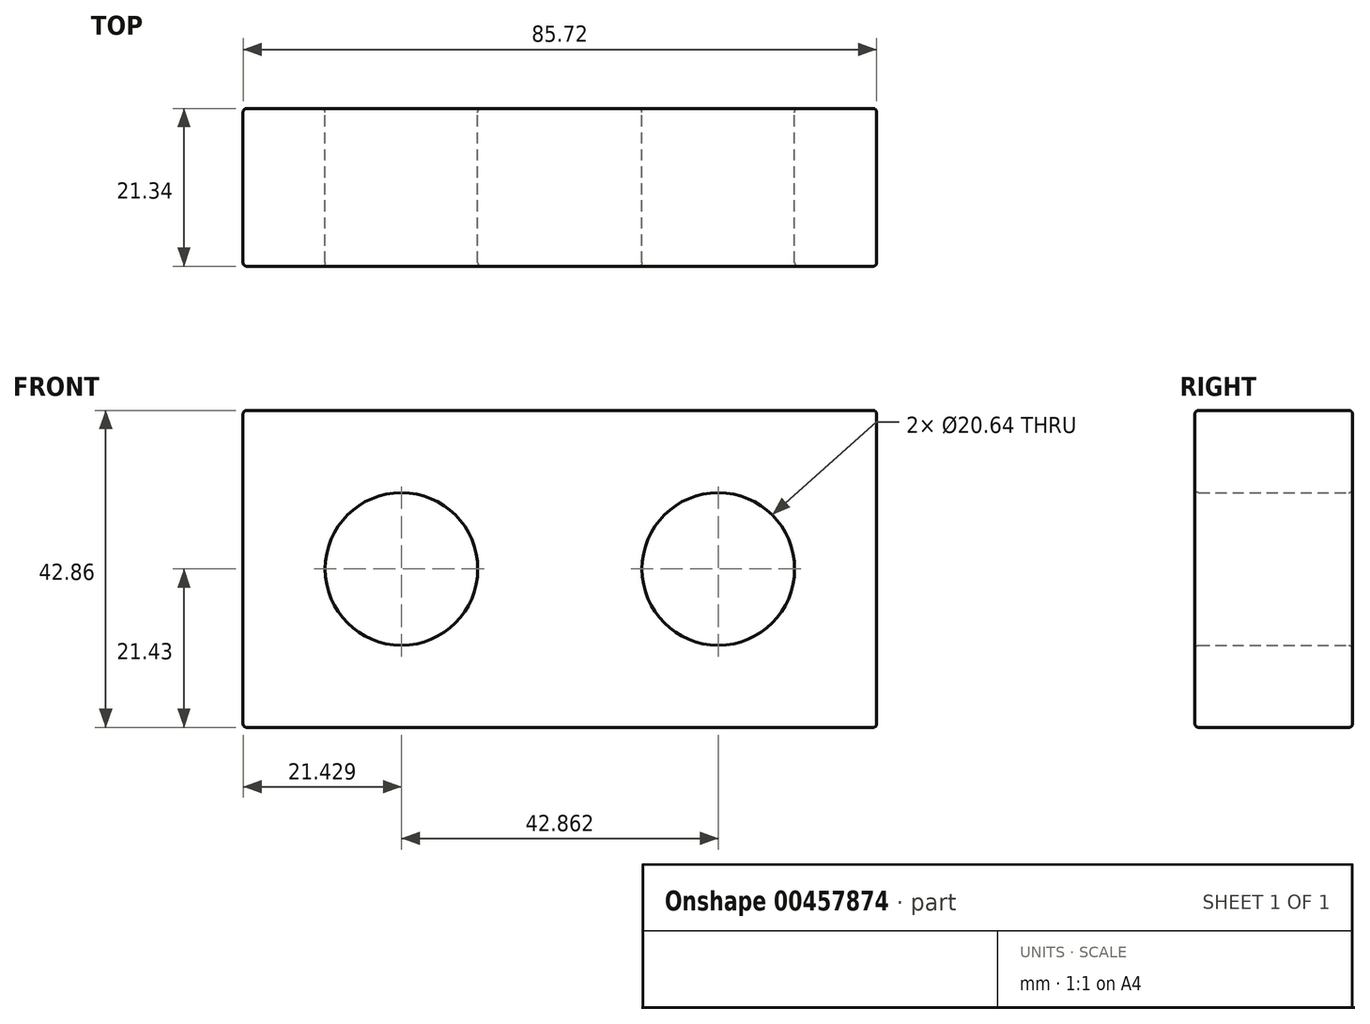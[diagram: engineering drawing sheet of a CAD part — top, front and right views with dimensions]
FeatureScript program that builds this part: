
annotation { "Feature Type Name" : "Feature", "Feature Type Description" : "" }
export const myFeature = defineFeature(function(context is Context, id is Id, definition is map)
    precondition{}
    {
        {
            var Q0;
            Q0=qCreatedBy(makeId("Front.planeOp"),FACE);
            var sketch = newSketch(context, id + "F0", { "sketchPlane" : qUnion([Q0])});
            skLineSegment(sketch, "E0.bottom", {"start": v(42.86, 21.43) * mm, "end": v(-42.86, 21.43) * mm});
            skLineSegment(sketch, "E0.top", {"start": v(42.86, -21.43) * mm, "end": v(-42.86, -21.43) * mm});
            skLineSegment(sketch, "E0.left", {"start": v(42.86, 21.43) * mm, "end": v(42.86, -21.43) * mm});
            skLineSegment(sketch, "E0.right", {"start": v(-42.86, 21.43) * mm, "end": v(-42.86, -21.43) * mm});
            skPoint(sketch, "E0.middle", {"position": v(0, 0) * mm});
            skLineSegment(sketch, "E1", {"start": v(-42.86, 0) * mm, "end": v(0, 0) * mm, "construction": true});
            skLineSegment(sketch, "E2", {"start": v(0, 0) * mm, "end": v(42.86, 0) * mm, "construction": true});
            skCircle(sketch, "E3", {"center": v(-21.43, 0) * mm, "radius": 10.32 * mm});
            skCircle(sketch, "E4", {"center": v(21.43, 0) * mm, "radius": 10.32 * mm});
            skSolve(sketch);
        }
        {
            var Q0;
            Q0 = qSketchRegion(id + "F0", true);
            extrude(context, id + "F1", {"entities" : qUnion([Q0]), "depth" : 21.34 * mm});
        }
        {
            var Q0;
            Q0=makeQuery(id+"F1.opExtrude","CAP_EDGE",EDGE,{"disambiguationData":[OSD([sQuery(id+"F0.wireOp",EDGE,"E0.bottom")])],"isStart":false});
            var Q1;
            Q1=makeQuery(id+"F1.opExtrude","CAP_EDGE",EDGE,{"disambiguationData":[OSD([sQuery(id+"F0.wireOp",EDGE,"E0.bottom")])],"isStart":true});
            var Q2;
            Q2=makeQuery(id+"F1.opExtrude","SWEPT_EDGE",EDGE,{"disambiguationData":[OSD([sQuery(id+"F0.wireOp",EDGE,"E0.bottom"),sQuery(id+"F0.wireOp",EDGE,"E0.right")])]});
            var Q3;
            Q3=makeQuery(id+"F1.opExtrude","SWEPT_EDGE",EDGE,{"disambiguationData":[OSD([sQuery(id+"F0.wireOp",EDGE,"E0.bottom"),sQuery(id+"F0.wireOp",EDGE,"E0.left")])]});
            var Q4;
            Q4=makeQuery(id+"F1.opExtrude","CAP_EDGE",EDGE,{"disambiguationData":[OSD([sQuery(id+"F0.wireOp",EDGE,"E0.left")])],"isStart":false});
            var Q5;
            Q5=makeQuery(id+"F1.opExtrude","CAP_EDGE",EDGE,{"disambiguationData":[OSD([sQuery(id+"F0.wireOp",EDGE,"E0.left")])],"isStart":true});
            var Q6;
            Q6=makeQuery(id+"F1.opExtrude","SWEPT_EDGE",EDGE,{"disambiguationData":[OSD([sQuery(id+"F0.wireOp",EDGE,"E0.top"),sQuery(id+"F0.wireOp",EDGE,"E0.left")])]});
            var Q7;
            Q7=makeQuery(id+"F1.opExtrude","CAP_EDGE",EDGE,{"disambiguationData":[OSD([sQuery(id+"F0.wireOp",EDGE,"E0.top")])],"isStart":false});
            var Q8;
            Q8=makeQuery(id+"F1.opExtrude","CAP_EDGE",EDGE,{"disambiguationData":[OSD([sQuery(id+"F0.wireOp",EDGE,"E0.right")])],"isStart":false});
            var Q9;
            Q9=makeQuery(id+"F1.opExtrude","CAP_EDGE",EDGE,{"disambiguationData":[OSD([sQuery(id+"F0.wireOp",EDGE,"E4")])],"isStart":false});
            var Q10;
            Q10=makeQuery(id+"F1.opExtrude","CAP_EDGE",EDGE,{"disambiguationData":[OSD([sQuery(id+"F0.wireOp",EDGE,"E3")])],"isStart":false});
            var Q11;
            Q11=makeQuery(id+"F1.opExtrude","SWEPT_EDGE",EDGE,{"disambiguationData":[OSD([sQuery(id+"F0.wireOp",EDGE,"E0.top"),sQuery(id+"F0.wireOp",EDGE,"E0.right")])]});
            var Q12;
            Q12=makeQuery(id+"F1.opExtrude","CAP_EDGE",EDGE,{"disambiguationData":[OSD([sQuery(id+"F0.wireOp",EDGE,"E0.right")])],"isStart":true});
            var Q13;
            Q13=makeQuery(id+"F1.opExtrude","CAP_EDGE",EDGE,{"disambiguationData":[OSD([sQuery(id+"F0.wireOp",EDGE,"E0.top")])],"isStart":true});
            var Q14;
            Q14=makeQuery(id+"F1.opExtrude","CAP_EDGE",EDGE,{"disambiguationData":[OSD([sQuery(id+"F0.wireOp",EDGE,"E3")])],"isStart":true});
            var Q15;
            Q15=makeQuery(id+"F1.opExtrude","CAP_EDGE",EDGE,{"disambiguationData":[OSD([sQuery(id+"F0.wireOp",EDGE,"E4")])],"isStart":true});
            fillet(context, id + "F2", {"entities" : qUnion([Q0, Q1, Q2, Q3, Q4, Q5, Q6, Q7, Q8, Q9, Q10, Q11, Q12, Q13, Q14, Q15]), "radius" : 0.5 * mm, "tangentPropagation" : true, "allowEdgeOverflow" : false});
        }
    });
